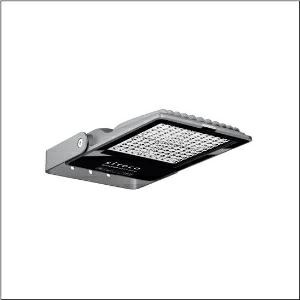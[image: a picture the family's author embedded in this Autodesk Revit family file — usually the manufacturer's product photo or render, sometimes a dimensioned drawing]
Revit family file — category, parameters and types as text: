
# Revit family: sicompact_r__31_mini___pl32_5xa7571f1k23_4385
name_source: partatom
category: Lighting Fixtures
units: mm (PartAtom-declared; Revit-internal decimal feet)

## family parameters
Cut with Voids When Loaded = No
Host = Face
Light Source = No
Part Type = Normal
Room Calculation Point = No
Round Connector Dimension = Use Diameter
Shared = No

## types (1)
- SiCompact® 31 mini  PL32 (1 x LED, 20000 lm, 130 W, 3000K)
    Apparent Load = 130 VA
    CIE Flux Codes = 32 69 98 100 100
    Color Rendering = 70
    Color Temperature = 3000K
    Default Elevation = 1800 mm
    Description = SiCompact® 31 mini, floodlight, primary light control with lens, of plastic, of toughened safety glass, transparent, light distribution: PL32, light emission: direct distribution, primary light characteristic: asymmetric, installation type: surface-mounted, LED, High Power LED, rated luminous flux: 20.000lm, luminous efficacy: 154lm/W, light colour: 730, colour temperature: 3000K, control gear: ECG, with cable, 3x 1.5mm², mains connection: 220..240V, AC, 50/60Hz, connection cable pre-assembled, cable length: 2m, rated input power: 130W, of diecast aluminium, specular, metallic grey (RAL 9006), length: 461mm, width: 261mm, height: 62mm, bracket, of sheet steel, coated, metallic grey (RAL 9006), ON/OFF, protection rating (complete): IP66, insulation class (complete): insulation class I (protective earthing), certification: CE, ENEC, impact resistance: IK08, permissible operating ambient temperature: -40..+45°C, packaging unit: 1 piece

Light Distribution: PL32
    Height = 62 mm  [stored 0.203412 ft]
    Lamp = 1 x LED
    Lamp Light Flux = 20000 lm
    Lamp Power = 130 W
    Lamp count = 1
    Length = 460 mm
    Luminous efficacy = 154 lm/W
    Manufacturer = Siteco
    ModVariant = No
    Model = 5XA7571F1K23
    Mounting Place = Wall
    Mounting Type = Surface mounted
    Number of Poles = 1
    OnlyDefault = Yes
    Power Factor = 1
    Product Name = SiCompact® 31 mini | PL32
    Product group = floodlight | wall mounted
    ProductGroupID = 2001
    Protection Class = Protection class I
    Protection Degree = IP 66
    RLX_Detail_Level = 1
    RLX_Emergency_Light_Flux = 0 lm
    RLX_Emergency_Type = 0
    RLX_Emergency_Type_DB = No
    RlxData = <blob elided: 126705 chars, md5=1e05a848>
    Socket = socket
    Standby Power = 0 W
    System Light Flux = 20000 lm
    System Power = 130 W
    Type Comments = Product without accessories
    Type Image = l_1006951.jpg
    URL = http://relux.com
    VarID = ---
    Voltage = 0 V
    Weight = 0.00 kg
    Width = 260 mm

note: [stored X ft] marks values corroborated as IEEE doubles in the binary element streams (Revit-internal decimal feet)

## geometry (parser evidence)
native form markers: Blend x4, Sweep x12
no freeform markers — native parametric forms only
